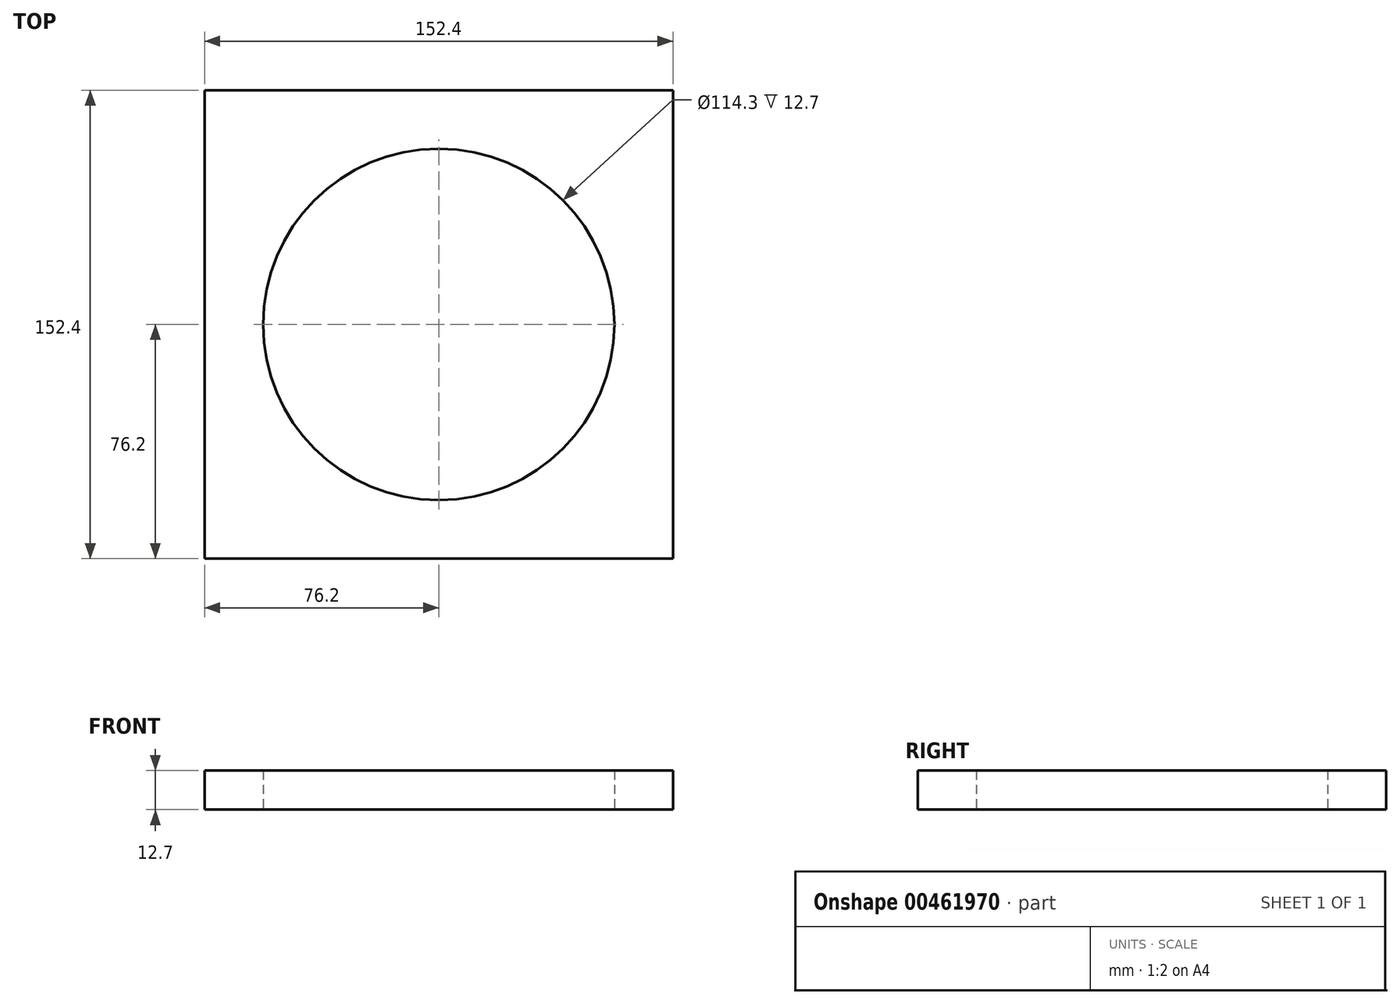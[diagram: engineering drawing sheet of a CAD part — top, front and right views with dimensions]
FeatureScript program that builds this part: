
annotation { "Feature Type Name" : "Feature", "Feature Type Description" : "" }
export const myFeature = defineFeature(function(context is Context, id is Id, definition is map)
    precondition{}
    {
        {
            var Q0;
            Q0=qCreatedBy(makeId("Top.planeOp"),FACE);
            var sketch = newSketch(context, id + "F0", { "sketchPlane" : qUnion([Q0])});
            skLineSegment(sketch, "E0.bottom", {"start": v(76.2, 76.2) * mm, "end": v(-76.2, 76.2) * mm});
            skLineSegment(sketch, "E0.top", {"start": v(76.2, -76.2) * mm, "end": v(-76.2, -76.2) * mm});
            skLineSegment(sketch, "E0.left", {"start": v(76.2, 76.2) * mm, "end": v(76.2, -76.2) * mm});
            skLineSegment(sketch, "E0.right", {"start": v(-76.2, 76.2) * mm, "end": v(-76.2, -76.2) * mm});
            skPoint(sketch, "E0.middle", {"position": v(0, 0) * mm});
            skCircle(sketch, "E1", {"center": v(0, 0) * mm, "radius": 57.15 * mm});
            skSolve(sketch);
        }
        {
            var Q0;
            Q0 = qSketchRegion(id + "F0", true);
            extrude(context, id + "F1", {"entities" : qUnion([Q0]), "depth" : 12.7 * mm});
        }
    });
